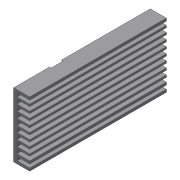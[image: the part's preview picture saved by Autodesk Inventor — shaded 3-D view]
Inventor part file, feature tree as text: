
AUTODESK INVENTOR PART (.ipt)
format: ipt  version: 2018 (Build 220112000, 112)  size: 175,104 bytes
history: native  units: mm
features: extrude x6, sketch x6, projected_geometry x3, mirror x1, pattern_linear x1
ambient origin geometry x8: Origin, YZ Plane, XZ Plane, XY Plane, X Axis, Y Axis, Z Axis, Center Point
bodies: Solid1 (feature_tree)
feature tree (17):
  extrude  "Extrusion1"  Depth=40.0mm
  extrude  "Extrusion2"  Depth=1.7mm
  mirror  "Mirror1"
  extrude  "Extrusion3"  Depth=2.2mm
  pattern_linear  "Rectangular Pattern1"  Spacing1=85.0mm  [1 undecoded]
  extrude  "Extrusion4"  Depth=3.82mm
  extrude  "Extrusion5"  Depth=1.0mm TaperAngle=0.0deg
  extrude  "Extrusion6"  Depth=1.0mm TaperAngle=0.0deg
  sketch  "Sketch1"  dims[d0=20.0mm d1=40.0mm]
  sketch  "Sketch2"  dims[d2=85.0mm d3=0.0mm d4=1.7mm]
  projected_geometry  "Projected Loop1"
  sketch  "Sketch3"  dims[d5=4.2mm d6=2.2mm]
  projected_geometry  "Projected Loop2"
  sketch  "Sketch4"  dims[d7=85.0mm d8=0.0mm]
  projected_geometry  "Projected Loop3"
  sketch  "Sketch5"  dims[d9=1.3mm]
  sketch  "Sketch7"  dims[d10=2.52mm d11=85.0mm d12=0.0mm d13=80.0mm d15=3.82mm d16=2.0mm d17=0.0mm d18=8.0mm d19=0.0mm d24=9.525mm d25=3.0mm d26=26.0mm d27=1.0mm d28=0.0mm]
note: 1 required parameter value undecoded (feature->parameter linkage not recoverable at this tier; creation-order binding heuristic only, values carry confidence <= 0.55)
